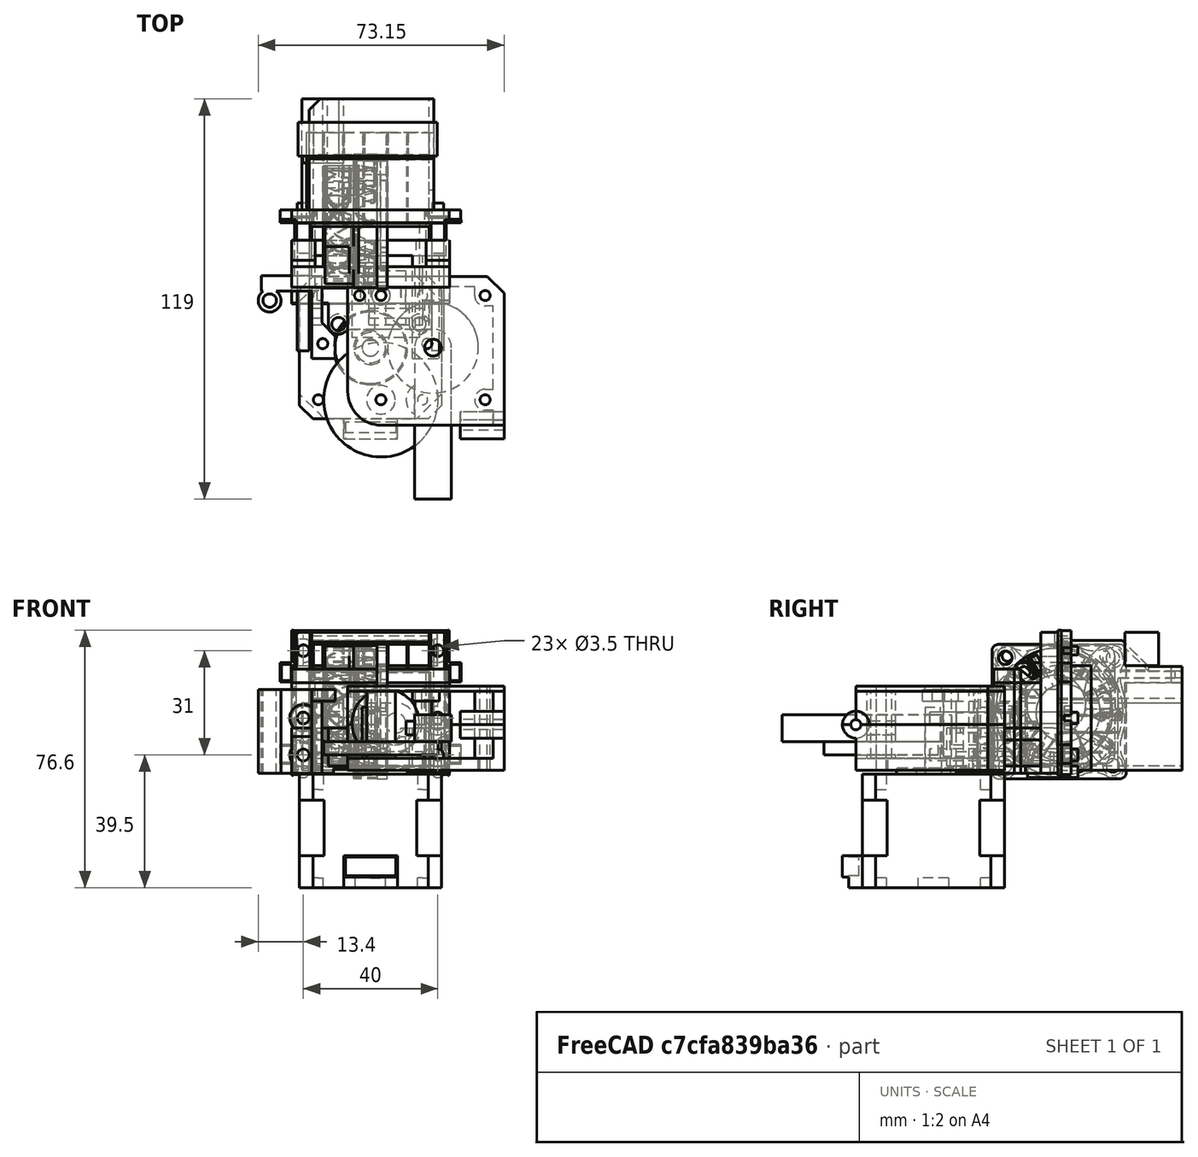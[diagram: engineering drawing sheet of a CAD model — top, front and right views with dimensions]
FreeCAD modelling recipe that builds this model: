
FCSTD DOCUMENT  (FreeCAD 0.17R9460 (Git))
Label: carriage_holder_proto_head
License: CC-BY 3.0
LicenseURL: http://creativecommons.org/licenses/by/3.0/
objects: Part::Box×86, Part::Cylinder×47, Part::MultiFuse×19, Part::Feature×16, Part::Cut×14, Mesh::Feature×6, App::DocumentObjectGroup×2, Part::Compound×2, Part::MultiCommon×1, Sketcher::SketchObject×1, Part::Extrusion×1, Part::Fillet×1, Drawing::FeatureViewPython×1, Drawing::FeaturePage×1, Part::Chamfer×1
note: 189 computed .brp shape members not serialized (recipe doc carries the construction recipe); baked Part::Feature solids carry a one-line shape summary decoded from their .brp

FEATURE [Part::Feature] Part__Feature  label="carriage holder base"
  Placement = pos=(0,4,-19.4607) rot=(1,0,0;1.5708rad)
  shape: bbox 53.76 x 4 x 42.8 mm, 26 faces (baked)
FEATURE [Part::Cylinder] Cylinder  label="cylinder for hole 1 - Motherboard"
  Angle = 360
  AttacherType = Attacher::AttachEngine3D
  Height = 15
  Placement = pos=(-20,6,17.5) rot=(1,0,0;1.5708rad)
  Radius = 1.75
FEATURE [Part::Cylinder] Cylinder001  label="cylinder for hole 2 - Motherboard"
  Angle = 360
  AttacherType = Attacher::AttachEngine3D
  Height = 15
  Placement = pos=(20,6,17.5) rot=(1,0,0;1.5708rad)
  Radius = 1.75
FEATURE [Part::Cylinder] Cylinder002  label="cylinder for hole 3 - Motherboard"
  Angle = 360
  AttacherType = Attacher::AttachEngine3D
  Height = 15
  Placement = pos=(-20,6,-18.5) rot=(1,0,0;1.5708rad)
  Radius = 1.75
FEATURE [Part::Cylinder] Cylinder003  label="cylinder for hole 4 - Motherboard"
  Angle = 360
  AttacherType = Attacher::AttachEngine3D
  Height = 15
  Placement = pos=(20,6,-18.5) rot=(1,0,0;1.5708rad)
  Radius = 1.75
FEATURE [Part::Cylinder] Cylinder008  label="cylinder for hole 9 - Groovemount L"
  Angle = 360
  AttacherType = Attacher::AttachEngine3D
  Height = 15
  Placement = pos=(-20,6,-2.5) rot=(1,0,0;1.5708rad)
  Radius = 1.75
FEATURE [Part::Cylinder] Cylinder009  label="cylinder for hole 10 - Groovemount R"
  Angle = 360
  AttacherType = Attacher::AttachEngine3D
  Height = 15
  Placement = pos=(20,6,-2.5) rot=(1,0,0;1.5708rad)
  Radius = 1.75
FEATURE [Part::Box] Box  label="shim L"
  AttacherType = Attacher::AttachEngine3D
  Height = 42
  Length = 4
  Placement = pos=(-22,-5,-19) rot=(0,0,1;0rad)
  Width = 6.1
FEATURE [Part::Box] Box001  label="shim R"
  AttacherType = Attacher::AttachEngine3D
  Height = 42
  Length = 4
  Placement = pos=(18,-5,-19) rot=(0,0,1;0rad)
  Width = 6.1
FEATURE [Part::Box] Box002  label="big aperture"
  AttacherType = Attacher::AttachEngine3D
  Height = 36
  Length = 32
  Placement = pos=(-16,-2,-18) rot=(0,0,1;0rad)
  Width = 10
FEATURE [Part::Cylinder] Cylinder010  label="cylinder for hole 2 nut seat"
  Angle = 360
  AttacherType = Attacher::AttachEngine3D
  Height = 2.5
  Placement = pos=(20,4,17.5) rot=(1,0,0;1.5708rad)
  Radius = 3.5
FEATURE [Part::Cylinder] Cylinder011  label="cylinder for hole 1 nut seat"
  Angle = 360
  AttacherType = Attacher::AttachEngine3D
  Height = 2.5
  Placement = pos=(-20,4,17.5) rot=(1,0,0;1.5708rad)
  Radius = 3.5
FEATURE [Part::Cylinder] Cylinder016  label="cylinder for hole 9 nut seat"
  Angle = 360
  AttacherType = Attacher::AttachEngine3D
  Height = 2
  Placement = pos=(-20,4,-2.5) rot=(1,0,0;1.5708rad)
  Radius = 3.5
FEATURE [Part::Cylinder] Cylinder017  label="cylinder for hole 10 nut seat"
  Angle = 360
  AttacherType = Attacher::AttachEngine3D
  Height = 2
  Placement = pos=(20,4,-2.5) rot=(1,0,0;1.5708rad)
  Radius = 3.5
FEATURE [Part::Box] Box003  label="shim subtractor L"
  AttacherType = Attacher::AttachEngine3D
  Height = 32
  Length = 3.4
  Placement = pos=(-27,1,-17) rot=(0,0,1;0rad)
  Width = 0.2
FEATURE [Part::Box] Box004  label="shim subtractor R"
  AttacherType = Attacher::AttachEngine3D
  Height = 32
  Length = 3.4
  Placement = pos=(23.6,1,-17) rot=(0,0,1;0rad)
  Width = 0.2
FEATURE [Part::Box] Box005  label="groovemount seat subtractor"
  AttacherType = Attacher::AttachEngine3D
  Height = 28
  Length = 36
  Placement = pos=(-18,-5,-17) rot=(0,0,1;0rad)
  Width = 5.2
FEATURE [Part::Box] Box006  label="Fan, screws and fan mount placeholder"
  AttacherType = Attacher::AttachEngine3D
  Height = 19
  Length = 35
  Placement = pos=(-17.5,0,3) rot=(0,0,1;0rad)
  Width = 35
FEATURE [Part::Box] Box007  label="Front intersector"
  AttacherType = Attacher::AttachEngine3D
  Height = 15
  Length = 56
  Placement = pos=(-28,-45,-20.5) rot=(0,0,1;0rad)
  Width = 49
FEATURE [Part::Cut] Cut001  label="groovemount E3D v6 high version"
FEATURE [Part::MultiCommon] Common  label="Front intersection"
  Shapes = -> [Cut001,Box007]
FEATURE [Part::Box] Box008  label="Left groovemount subtractor"
  AttacherType = Attacher::AttachEngine3D
  Height = 12
  Length = 10
  Placement = pos=(-32,-5,-17) rot=(0,0,1;0rad)
  Width = 5
FEATURE [Part::Box] Box009  label="Right groovemount subtractor"
  AttacherType = Attacher::AttachEngine3D
  Height = 12
  Length = 10
  Placement = pos=(22,-5,-17) rot=(0,0,1;0rad)
  Width = 5
FEATURE [Part::MultiFuse] Fusion  label="holes"
  Shapes = -> [Cylinder001,Cylinder,Cylinder008,Cylinder009,Box002,Cylinder010,Cylinder011,Cylinder016,Cylinder017,Box003,Box004,Box006,Box008,Box009]
FEATURE [Part::Box] Box010  label="Left groovemount adder"
  AttacherType = Attacher::AttachEngine3D
  Height = 11.25
  Length = 2
  Placement = pos=(-18.5,-5,-16.75) rot=(0,0,1;0rad)
  Width = 5
FEATURE [Part::Box] Box011  label="Right groovemount adder"
  AttacherType = Attacher::AttachEngine3D
  Height = 11.25
  Length = 2
  Placement = pos=(16.5,-5,-16.75) rot=(0,0,1;0rad)
  Width = 5
FEATURE [Part::MultiFuse] Fusion001  label="body"
  Shapes = -> [Part__Feature,Box001,Box,Common,Box010,Box011]
FEATURE [Part::Cut] Cut  label="carriage with shim and holes"
  Base = -> Fusion001
  Tool = -> Fusion
FEATURE [Part::Box] Box012  label="all area - outside "
  AttacherType = Attacher::AttachEngine3D
  Height = 38.6
  Length = 37
  Placement = pos=(-18.2,0,-18) rot=(0,0,1;0rad)
  Width = 37
FEATURE [Part::Box] Box014  label="safe area 1 - inside"
  AttacherType = Attacher::AttachEngine3D
  Height = 36
  Length = 25.4
  Placement = pos=(-8,0,-16.6) rot=(0,0,1;0rad)
  Width = 37
FEATURE [Part::Box] Box015  label="safe area 2 - inside"
  AttacherType = Attacher::AttachEngine3D
  Height = 16
  Length = 9
  Placement = pos=(-17,0,3.4) rot=(0,0,1;0rad)
  Width = 37
FEATURE [Part::Feature] Part__Feature001  label="carriage holder base001"
  Placement = pos=(0,4,-19.4607) rot=(1,0,0;1.5708rad)
  shape: bbox 53.76 x 4 x 42.8 mm, 26 faces (baked)
FEATURE [Part::Box] Box016  label="top remover"
  AttacherType = Attacher::AttachEngine3D
  Height = 60
  Length = 60
  Placement = pos=(-31,0,-29) rot=(0,0,1;0rad)
  Width = 0.1
FEATURE [Part::Box] Box017  label="recess"
  AttacherType = Attacher::AttachEngine3D
  Height = 6
  Length = 6
  Placement = pos=(-20.2,18,2) rot=(0,0,1;0rad)
  Width = 19
FEATURE [Part::Box] Box018  label="raspicam collision area - outside001"
  AttacherType = Attacher::AttachEngine3D
  Height = 20
  Length = 11
  Placement = pos=(-20.4,0,-18) rot=(0,0,1;0rad)
  Width = 37
FEATURE [Part::Cut] Cut004  label="raspicam_extra"
  Base = -> Box018
  Tool = -> Box017
FEATURE [Part::Box] Box020  label="recess_base"
  AttacherType = Attacher::AttachEngine3D
  Height = 6
  Length = 4
  Placement = pos=(-18.2,18,2) rot=(0,0,1;0rad)
  Width = 2
FEATURE [Part::Box] Box021  label="support for recess base X1"
  AttacherType = Attacher::AttachEngine3D
  Height = 0.4
  Length = 4
  Placement = pos=(-17,0.1,9) rot=(0,0,1;0rad)
  Width = 18
FEATURE [Part::Box] Box022  label="support for recess base Y1"
  AttacherType = Attacher::AttachEngine3D
  Height = 6
  Length = 0.4
  Placement = pos=(-13.2,0.1,3.4) rot=(0,0,1;0rad)
  Width = 18
FEATURE [Part::Box] Box023  label="raspicam collision area - outside lower"
  AttacherType = Attacher::AttachEngine3D
  Height = 20
  Length = 9
  Placement = pos=(-18.4,20,-18) rot=(0,0,1;0rad)
  Width = 34
FEATURE [Part::Box] Box024  label="recess001"
  AttacherType = Attacher::AttachEngine3D
  Height = 6
  Length = 6
  Placement = pos=(-20.2,18,2) rot=(0,0,1;0rad)
  Width = 19
FEATURE [Part::Box] Box025  label="recess wall 1"
  AttacherType = Attacher::AttachEngine3D
  Height = 6
  Length = 1.4
  Placement = pos=(-14.2,18,2) rot=(0,0,1;0rad)
  Width = 19
FEATURE [Part::Box] Box026  label="recess wall 2"
  AttacherType = Attacher::AttachEngine3D
  Height = 1.4
  Length = 5.4
  Placement = pos=(-18.2,18,8) rot=(0,0,1;0rad)
  Width = 19
FEATURE [Part::Box] Box027  label="Raspicam chamfer"
  AttacherType = Attacher::AttachEngine3D
  Height = 15
  Length = 13
  Placement = pos=(-22,30,7) rot=(0,0,1;0.785398rad)
  Width = 10
FEATURE [Part::Box] Box028  label="Rear panel chamfer"
  AttacherType = Attacher::AttachEngine3D
  Height = 11
  Length = 41.4
  Placement = pos=(-21.6,27,12.81) rot=(1,0,0;0.785398rad)
  Width = 10
FEATURE [Part::Box] Box029  label="Rear panel recess template"
  AttacherType = Attacher::AttachEngine3D
  Height = 31
  Length = 1.4
  Placement = pos=(17.4,0,-18) rot=(0,0,1;0rad)
  Width = 10
FEATURE [Part::Box] Box030  label="Rear panel recess"
  AttacherType = Attacher::AttachEngine3D
  Height = 7.8
  Length = 41.4
  Placement = pos=(-21.6,27,12.8) rot=(0,0,1;0rad)
  Width = 10
FEATURE [Part::MultiFuse] Fusion004  label="Extra subtractions"
  Shapes = -> [Box027,Box030]
FEATURE [Part::Box] Box031  label="Rear panel chamfer template"
  AttacherType = Attacher::AttachEngine3D
  Height = 10
  Length = 41.4
  Placement = pos=(-21.6,20,13) rot=(0,0,1;0rad)
  Width = 10
FEATURE [Part::Box] Box032  label="Rear panel wall vs front"
  AttacherType = Attacher::AttachEngine3D
  Height = 1.4
  Length = 35.4
  Placement = pos=(-18,27,11.4) rot=(0,0,1;0rad)
  Width = 10
FEATURE [Sketcher::SketchObject] Sketch
  MapMode = 5
  Placement = pos=(-19,27,11.4) rot=(0.57735,0.57735,0.57735;2.0944rad)
  sketch-geometry (4):
    g0: LineSegment StartX=-6.61145 StartY=8.01145 StartZ=0 EndX=0 EndY=1.4 EndZ=0
    g1: LineSegment StartX=0 StartY=1.4 StartZ=0 EndX=0 EndY=0 EndZ=0
    g2: LineSegment StartX=0 StartY=0 StartZ=0 EndX=-8.01145 EndY=8.01145 EndZ=0
    g3: LineSegment StartX=-8.01145 StartY=8.01145 StartZ=0 EndX=-6.61145 EndY=8.01145 EndZ=0
  constraints (11):
    c: PointOnObject(g0,g-2)
    c: Coincident(g0,g1)
    c: Coincident(g1,g-1)
    c: Coincident(g1,g2)
    c: Coincident(g2,g3)
    c: Coincident(g3,g0)
    c: DistanceY(g1,g1) = 1.4
    c: DistanceX(g3,g3) = 1.4
    c: Parallel(g0,g2)
    c: Angle(g-1,g2) = 2.35619
    c: Distance(g0,g0) = 9.35
FEATURE [Part::Extrusion] Extrude  label="Rear panel angled"
  Base = -> Sketch
  Dir = (36,0,0)
  DirMode = 0
  FaceMakerClass = Part::FaceMakerExtrusion
  LengthFwd = 0
  LengthRev = 0
  Placement = pos=(1,0,0) rot=(0,0,1;0rad)
  Solid = true
  Symmetric = false
FEATURE [Part::Box] Box033  label="support X1 for rear panel angled"
  AttacherType = Attacher::AttachEngine3D
  Height = 0.4
  Length = 36.4
  Placement = pos=(-19,0.1,11.4) rot=(0,0,1;0rad)
  Width = 27
FEATURE [Part::Box] Box034  label="support Y1 for rear panel angled"
  AttacherType = Attacher::AttachEngine3D
  Height = 9
  Length = 0.4
  Placement = pos=(-14.2,0.1,11.4) rot=(0,0,1;0rad)
  Width = 27
FEATURE [Part::Box] Box035  label="support Y2 for rear panel angled"
  AttacherType = Attacher::AttachEngine3D
  Height = 9
  Length = 0.4
  Placement = pos=(-8.2,0.1,11.4) rot=(0,0,1;0rad)
  Width = 27
FEATURE [Part::Box] Box036  label="support Y3 for rear panel angled"
  AttacherType = Attacher::AttachEngine3D
  Height = 9
  Length = 0.4
  Placement = pos=(4.8,0.1,11.4) rot=(0,0,1;0rad)
  Width = 27
FEATURE [Part::Box] Box037  label="support Y4 for rear panel angled"
  AttacherType = Attacher::AttachEngine3D
  Height = 9
  Length = 0.4
  Placement = pos=(-2.2,0.1,11.4) rot=(0,0,1;0rad)
  Width = 27
FEATURE [Part::Box] Box038  label="support Y5 for rear panel angled"
  AttacherType = Attacher::AttachEngine3D
  Height = 9
  Length = 0.4
  Placement = pos=(10.8,0.1,11.4) rot=(0,0,1;0rad)
  Width = 27
FEATURE [Part::MultiFuse] Fusion005  label="supports for rear panel angled"
  Shapes = -> [Box033,Box037,Box036,Box035,Box034,Box038]
FEATURE [Part::Cut] Cut006  label="supports for rear panel angled - chamfered"
  Base = -> Fusion005
  Tool = -> Box028
FEATURE [Mesh::Feature] chinese_long_distance_hotend
  Placement = pos=(1.6,0,1.6) rot=(0,1,0;3.14159rad)
FEATURE [Part::Box] Box039  label="recess_base 2"
  AttacherType = Attacher::AttachEngine3D
  Height = 20
  Length = 12.2
  Placement = pos=(-20.2,18,-18) rot=(0,0,1;0rad)
  Width = 2
FEATURE [Part::Box] Box040  label="top on raspicam area "
  AttacherType = Attacher::AttachEngine3D
  Height = 20
  Length = 11
  Placement = pos=(-17,-16,-16.6) rot=(0,0,1;0rad)
  Width = 34
FEATURE [Part::Box] Box041  label="support for recess base X2"
  AttacherType = Attacher::AttachEngine3D
  Height = 0.4
  Length = 9
  Placement = pos=(-17,0.1,3) rot=(0,0,1;0rad)
  Width = 18
FEATURE [Part::Box] Box042  label="support for recess base X3"
  AttacherType = Attacher::AttachEngine3D
  Height = 0.4
  Length = 10
  Placement = pos=(-18,0.1,-2) rot=(0,0,1;0rad)
  Width = 18
FEATURE [Part::Box] Box043  label="support for recess base X4"
  AttacherType = Attacher::AttachEngine3D
  Height = 0.4
  Length = 10
  Placement = pos=(-18,0.1,-13) rot=(0,0,1;0rad)
  Width = 18
FEATURE [Part::Box] Box044  label="support for recess base X5"
  AttacherType = Attacher::AttachEngine3D
  Height = 0.4
  Length = 9
  Placement = pos=(-17,0.1,-7) rot=(0,0,1;0rad)
  Width = 18
FEATURE [Part::Box] Box045  label="support for recess base Y2"
  AttacherType = Attacher::AttachEngine3D
  Height = 20
  Length = 0.4
  Placement = pos=(-8.4,0.1,-16.6) rot=(0,0,1;0rad)
  Width = 18
FEATURE [Part::MultiFuse] Fusion006  label="supports for recess base"
  Shapes = -> [Box041,Box045,Box044,Box042,Box043,Box021,Box022]
FEATURE [Part::Cylinder] Cylinder018  label="cylinder for hole 2 nut seat001"
  Angle = 360
  AttacherType = Attacher::AttachEngine3D
  Height = 2.5
  Placement = pos=(20,4,17.5) rot=(1,0,0;1.5708rad)
  Radius = 3.5
FEATURE [Part::Cylinder] Cylinder019  label="cylinder for hole 1 nut seat001"
  Angle = 360
  AttacherType = Attacher::AttachEngine3D
  Height = 2.5
  Placement = pos=(-20,4,17.5) rot=(1,0,0;1.5708rad)
  Radius = 3.5
FEATURE [Part::Cylinder] Cylinder020  label="cylinder for hole 1 - Motherboard001"
  Angle = 360
  AttacherType = Attacher::AttachEngine3D
  Height = 15
  Placement = pos=(-20,6,17.5) rot=(1,0,0;1.5708rad)
  Radius = 1.75
FEATURE [Part::Cylinder] Cylinder021  label="cylinder for hole 2 - Motherboard001"
  Angle = 360
  AttacherType = Attacher::AttachEngine3D
  Height = 15
  Placement = pos=(20,6,17.5) rot=(1,0,0;1.5708rad)
  Radius = 1.75
FEATURE [Part::Box] Box046  label="shim R001"
  AttacherType = Attacher::AttachEngine3D
  Height = 42
  Length = 5
  Placement = pos=(17.5,-5,-19) rot=(0,0,1;0rad)
  Width = 5.1
FEATURE [Part::Box] Box047  label="shim L001"
  AttacherType = Attacher::AttachEngine3D
  Height = 42
  Length = 5
  Placement = pos=(-22.5,-5,-19) rot=(0,0,1;0rad)
  Width = 5.1
FEATURE [Part::Box] Box048  label="shim back"
  AttacherType = Attacher::AttachEngine3D
  Height = 3
  Length = 44
  Placement = pos=(-22,-1,20) rot=(0,0,1;0rad)
  Width = 1.1
FEATURE [Part::Box] Box049  label="shim front"
  AttacherType = Attacher::AttachEngine3D
  Height = 2
  Length = 44
  Placement = pos=(-22,-1,-19) rot=(0,0,1;0rad)
  Width = 1.1
FEATURE [Part::MultiFuse] Fusion007  label="superstructure"
  Shapes = -> [Box046,Box048,Box047,Box049]
FEATURE [Part::Cylinder] Cylinder022  label="cylinder for hole 1 - Motherboard002"
  Angle = 360
  AttacherType = Attacher::AttachEngine3D
  Height = 44
  Placement = pos=(-20,6,17.5) rot=(1,0,0;1.5708rad)
  Radius = 1.75
FEATURE [Part::Cylinder] Cylinder023  label="cylinder for hole 2 - Motherboard002"
  Angle = 360
  AttacherType = Attacher::AttachEngine3D
  Height = 44
  Placement = pos=(20,6,17.5) rot=(1,0,0;1.5708rad)
  Radius = 1.75
FEATURE [Part::Cylinder] Cylinder024  label="cylinder for hole 9 - Groovemount L001"
  Angle = 360
  AttacherType = Attacher::AttachEngine3D
  Height = 44
  Placement = pos=(-20,6,-2.5) rot=(1,0,0;1.5708rad)
  Radius = 1.75
FEATURE [Part::Cylinder] Cylinder025  label="cylinder for hole 10 - Groovemount R001"
  Angle = 360
  AttacherType = Attacher::AttachEngine3D
  Height = 44
  Placement = pos=(20,6,-2.5) rot=(1,0,0;1.5708rad)
  Radius = 1.75
FEATURE [Part::Cylinder] Cylinder026  label="cylinder for hole 9 nut seat001"
  Angle = 360
  AttacherType = Attacher::AttachEngine3D
  Height = 2
  Placement = pos=(-20,4,-2.5) rot=(1,0,0;1.5708rad)
  Radius = 3.5
FEATURE [Part::Cylinder] Cylinder027  label="cylinder for hole 10 nut seat001"
  Angle = 360
  AttacherType = Attacher::AttachEngine3D
  Height = 2
  Placement = pos=(20,4,-2.5) rot=(1,0,0;1.5708rad)
  Radius = 3.5
FEATURE [Part::Cylinder] Cylinder028  label="cylinder for hole 9 - Groovemount L002"
  Angle = 360
  AttacherType = Attacher::AttachEngine3D
  Height = 15
  Placement = pos=(-20,6,-2.5) rot=(1,0,0;1.5708rad)
  Radius = 1.75
FEATURE [Part::Cylinder] Cylinder029  label="cylinder for hole 10 - Groovemount R002"
  Angle = 360
  AttacherType = Attacher::AttachEngine3D
  Height = 15
  Placement = pos=(20,6,-2.5) rot=(1,0,0;1.5708rad)
  Radius = 1.75
FEATURE [Part::Cylinder] Cylinder030  label="cylinder for hole 3 - Motherboard001"
  Angle = 360
  AttacherType = Attacher::AttachEngine3D
  Height = 15
  Placement = pos=(-20,6,-13.5) rot=(1,0,0;1.5708rad)
  Radius = 1.75
FEATURE [Part::Cylinder] Cylinder031  label="cylinder for hole 4 - Motherboard001"
  Angle = 360
  AttacherType = Attacher::AttachEngine3D
  Height = 15
  Placement = pos=(20,6,-13.5) rot=(1,0,0;1.5708rad)
  Radius = 1.75
FEATURE [Part::Cylinder] Cylinder032  label="cylinder for hole 9 nut seat002"
  Angle = 360
  AttacherType = Attacher::AttachEngine3D
  Height = 2
  Placement = pos=(-20,4,-13.5) rot=(1,0,0;1.5708rad)
  Radius = 3.5
FEATURE [Part::Cylinder] Cylinder033  label="cylinder for hole 10 nut seat002"
  Angle = 360
  AttacherType = Attacher::AttachEngine3D
  Height = 2
  Placement = pos=(20,4,-13.5) rot=(1,0,0;1.5708rad)
  Radius = 3.5
FEATURE [Part::MultiFuse] Fusion002  label="safe area holes"
  Shapes = -> [Box014,Box015,Box016,Box023,Box024,Box028,Fusion004,Box040,Cylinder018,Cylinder019,Cylinder020,Cylinder021,Cylinder027,Cylinder026,Cylinder028,Cylinder029,Cylinder030,Cylinder031,Cylinder032,Cylinder033]
FEATURE [Part::Cut] Cut002  label="safe area protector"
  Base = -> Box012
  Tool = -> Fusion002
FEATURE [Part::Cut] Cut003  label="carriage holder base with safe area aperture"
  Base = -> Part__Feature001
  Tool = -> Fusion002
FEATURE [Part::Cylinder] Cylinder034  label="cylinder for hole 3 - Motherboard002"
  Angle = 360
  AttacherType = Attacher::AttachEngine3D
  Height = 44
  Placement = pos=(-20,6,-13.5) rot=(1,0,0;1.5708rad)
  Radius = 1.75
FEATURE [Part::Cylinder] Cylinder035  label="cylinder for hole 4 - Motherboard002"
  Angle = 360
  AttacherType = Attacher::AttachEngine3D
  Height = 44
  Placement = pos=(20,6,-13.5) rot=(1,0,0;1.5708rad)
  Radius = 1.75
FEATURE [Part::MultiFuse] Fusion008  label="superstructure holes"
  Shapes = -> [Cylinder022,Cylinder023,Cylinder024,Cylinder025,Cylinder034,Cylinder035]
FEATURE [Part::Cut] Cut007  label="superstructure with holes"
  Base = -> Fusion007
  Tool = -> Fusion008
FEATURE [Mesh::Feature] k3dpkr_rc_1_0_x_carriage  label="k3dpkr-rc-1.0-x-carriage"
  Placement = pos=(-466,-28,-403) rot=(-1,0,0;1.5708rad)
FEATURE [Part::Box] Box050  label="coldend carriage plate"
  AttacherType = Attacher::AttachEngine3D
  Height = 17
  Length = 47
  Placement = pos=(-23.5,-19,-9) rot=(0,0,1;0rad)
  Width = 6.1
FEATURE [Part::Cylinder] Cylinder036  label="coldend carriage plate hole"
  Angle = 360
  AttacherType = Attacher::AttachEngine3D
  Height = 34
  Placement = pos=(4.5,0,-4) rot=(1,0,0;1.5708rad)
  Radius = 10
FEATURE [Part::MultiFuse] Fusion009  label="coldend carriage holes"
  Shapes = -> [Cylinder024,Cylinder025,Cylinder034,Cylinder035,Cylinder036]
FEATURE [Part::Box] Box051  label="coldend cariage structure R"
  AttacherType = Attacher::AttachEngine3D
  Height = 17
  Length = 7
  Placement = pos=(16.5,-12.9,-9) rot=(0,0,1;0rad)
  Width = 7.9
FEATURE [Part::Box] Box052  label="coldend cariage structure L"
  AttacherType = Attacher::AttachEngine3D
  Height = 17
  Length = 7
  Placement = pos=(-23.5,-12.9,-9) rot=(0,0,1;0rad)
  Width = 7.9
FEATURE [Part::MultiFuse] Fusion010  label="coldend attach structure"
  Shapes = -> [Box051,Box052,Box050]
FEATURE [Part::Cut] Cut008  label="coldend attach structure with holes"
  Base = -> Fusion010
  Tool = -> Fusion009
FEATURE [Part::Feature] Part__Feature200  label="Part 003"
  shape: bbox 30 x 30.5 x 10.5 mm, 33 faces (baked)
FEATURE [Part::Feature] Part__Feature201  label="Part 004"
  shape: bbox 28.66 x 28.3 x 8.25 mm, 39 faces (baked)
FEATURE [Part::MultiFuse] Fusion014  label="30x30x10 coldend fan"
  Placement = pos=(-14,2,-1) rot=(0,1,0;1.5708rad)
  Shapes = -> [Part__Feature201,Part__Feature200]
FEATURE [Part::Cylinder] Cylinder037  label="jhead hole"
  Angle = 360
  AttacherType = Attacher::AttachEngine3D
  Height = 34
  Placement = pos=(4.5,0,-4) rot=(1,0,0;1.5708rad)
  Radius = 6
FEATURE [Part::Box] Box053  label="jhead retention plate body"
  AttacherType = Attacher::AttachEngine3D
  Height = 27
  Length = 47
  Placement = pos=(-23.5,-24,-19) rot=(0,0,1;0rad)
  Width = 5
FEATURE [Part::Box] Box054  label="jhead retention plate chamfer L"
  AttacherType = Attacher::AttachEngine3D
  Height = 14
  Length = 37
  Placement = pos=(-32.5,-24,-17) rot=(0,1,0;0.314159rad)
  Width = 5
FEATURE [Part::Box] Box055  label="jhead retention plate chamfer R"
  AttacherType = Attacher::AttachEngine3D
  Height = 11
  Length = 22
  Placement = pos=(16.5,-24,-27) rot=(0,-1,0;0.785398rad)
  Width = 5
FEATURE [Part::Box] Box056  label="jhead retention plate slide in hole"
  AttacherType = Attacher::AttachEngine3D
  Height = 31
  Length = 12
  Placement = pos=(-1.5,-24,-35) rot=(0,0,1;0rad)
  Width = 5
FEATURE [Part::MultiFuse] Fusion015  label="jhead retention plate holes"
  Shapes = -> [Cylinder025,Cylinder024,Cylinder037,Box054,Box055,Box056]
FEATURE [Part::Cut] Cut009  label="jhead retention plate with holes"
  Base = -> Box053
  Tool = -> Fusion015
FEATURE [Part::Fillet] Fillet  label="jhead retention plate with holes and fillets"
  Base = -> Cut009
  Edges = 6 edges r=3: [Edge2,Edge4,Edge15,Edge24,Edge27,Edge28]
FEATURE [Mesh::Feature] Pico
  Placement = pos=(12,36,-11) rot=(0,0,1;3.14159rad)
FEATURE [Part::Box] Box057  label="jhead lock plate"
  AttacherType = Attacher::AttachEngine3D
  Height = 11
  Length = 47
  Placement = pos=(-23.5,-24,-18) rot=(0,0,1;0rad)
  Width = 5
FEATURE [Part::Cut] Cut010  label="jhead lock plate coupled with retention plate"
  Base = -> Box057
  Placement = pos=(0,0,-1) rot=(0,0,1;0rad)
  Tool = -> Fillet
FEATURE [Part::MultiFuse] Fusion016  label="jhead lock plate holes"
  Shapes = -> [Cylinder037,Cylinder035,Cylinder034]
FEATURE [Part::Cut] Cut011  label="jhead retention plates - lock and retention"
  Base = -> Cut010
  Tool = -> Fusion016
FEATURE [Part::Box] Box058  label="support for lock pins XL1"
  AttacherType = Attacher::AttachEngine3D
  Height = 0.4
  Length = 5
  Placement = pos=(-26.8,0.1,8.2) rot=(0,0,1;0rad)
  Width = 1
FEATURE [Part::Box] Box059  label="support for lock pins YL1"
  AttacherType = Attacher::AttachEngine3D
  Height = 43.2
  Length = 0.4
  Placement = pos=(-23.4,0.1,-19.6) rot=(0,0,1;0rad)
  Width = 1
FEATURE [Part::Box] Box060  label="support for lock pins YR1"
  AttacherType = Attacher::AttachEngine3D
  Height = 43.2
  Length = 0.4
  Placement = pos=(23,0.1,-19.6) rot=(0,0,1;0rad)
  Width = 1
FEATURE [Part::Box] Box061  label="support for lock pins YL2"
  AttacherType = Attacher::AttachEngine3D
  Height = 5.7
  Length = 0.4
  Placement = pos=(-26.9,0.1,8.2) rot=(0,0,1;0rad)
  Width = 1
FEATURE [Part::Box] Box062  label="support for lock pins XL2"
  AttacherType = Attacher::AttachEngine3D
  Height = 0.4
  Length = 5
  Placement = pos=(-26.8,0.1,13.5) rot=(0,0,1;0rad)
  Width = 1
FEATURE [Part::Box] Box063  label="support for lock pins XL3"
  AttacherType = Attacher::AttachEngine3D
  Height = 0.4
  Length = 5
  Placement = pos=(-26.8,0.1,-10.8) rot=(0,0,1;0rad)
  Width = 1
FEATURE [Part::Box] Box064  label="support for lock pins XL4"
  AttacherType = Attacher::AttachEngine3D
  Height = 0.4
  Length = 5
  Placement = pos=(-26.8,0.1,-16.1) rot=(0,0,1;0rad)
  Width = 1
FEATURE [Part::Box] Box065  label="support for lock pins YL3"
  AttacherType = Attacher::AttachEngine3D
  Height = 5.7
  Length = 0.4
  Placement = pos=(-26.9,0.1,-16.1) rot=(0,0,1;0rad)
  Width = 1
FEATURE [Part::Box] Box066  label="support for lock pins XR1"
  AttacherType = Attacher::AttachEngine3D
  Height = 0.4
  Length = 5
  Placement = pos=(22,0.1,8.2) rot=(0,0,1;0rad)
  Width = 1
FEATURE [Part::Box] Box067  label="support for lock pins XR2"
  AttacherType = Attacher::AttachEngine3D
  Height = 0.4
  Length = 5
  Placement = pos=(22,0.1,13.5) rot=(0,0,1;0rad)
  Width = 1
FEATURE [Part::Box] Box068  label="support for lock pins XR3"
  AttacherType = Attacher::AttachEngine3D
  Height = 0.4
  Length = 5
  Placement = pos=(22,0.1,-10.8) rot=(0,0,1;0rad)
  Width = 1
FEATURE [Part::Box] Box069  label="support for lock pins XR4"
  AttacherType = Attacher::AttachEngine3D
  Height = 0.4
  Length = 5
  Placement = pos=(22,0.1,-16.1) rot=(0,0,1;0rad)
  Width = 1
FEATURE [Part::Box] Box070  label="support for lock pins YR2"
  AttacherType = Attacher::AttachEngine3D
  Height = 5.7
  Length = 0.4
  Placement = pos=(26.6,0.1,8.2) rot=(0,0,1;0rad)
  Width = 1
FEATURE [Part::Box] Box071  label="support for lock pins YR3"
  AttacherType = Attacher::AttachEngine3D
  Height = 5.7
  Length = 0.4
  Placement = pos=(26.6,0.1,-16.1) rot=(0,0,1;0rad)
  Width = 1
FEATURE [Part::MultiFuse] Fusion017  label="support for lock pins"
  Shapes = -> [Box059,Box070,Box065,Box068,Box062,Box063,Box060,Box061,Box066,Box067,Box064,Box069,Box071,Box058]
FEATURE [Part::MultiFuse] Fusion003  label="carriage holder base with safe area protector"
  Shapes = -> [Cut003,Cut002,Box020,Box025,Box026,Box032,Extrude,Fusion006,Fusion017]
FEATURE [Part::Cut] Cut005  label="carriage holder base with safe area protector and extra subtractions"
  Base = -> Fusion003
  Tool = -> Box027
FEATURE [Drawing::FeatureViewPython] ViewCut005  # drawing view (typed FeaturePython)
  AlwaysOn = false
  Direction = (0,0,0)
  FillStyle = 0
  FontSize = 12
  LineSpacing = 0
  LineStyle = 0
  LineWidth = 0.35
  Rotation = 0
  Scale = 20
  Source = -> Cut005
  ViewResult = <blob: 93087 chars omitted>
  Visible = false
  X = 200
  Y = 100
FEATURE [Drawing::FeaturePage] Page
  EditableTexts = AUTHOR NAME | CREATION DATE | SUPERVISOR NAME | CHECK DATE | SCALE | WEIGHT | NUMBER | SHEET | TITLE | SUBTITLE
  Group = -> [ViewCut005]
  Template = <path>
FEATURE [Part::Cylinder] Cylinder038  label="cylinder for hole 9 - Groovemount L003"
  Angle = 360
  AttacherType = Attacher::AttachEngine3D
  Height = 44
  Placement = pos=(-20,6,-2.5) rot=(1,0,0;1.5708rad)
  Radius = 1.75
FEATURE [Part::Cylinder] Cylinder039  label="cylinder for hole 10 - Groovemount R003"
  Angle = 360
  AttacherType = Attacher::AttachEngine3D
  Height = 44
  Placement = pos=(20,6,-2.5) rot=(1,0,0;1.5708rad)
  Radius = 1.75
FEATURE [Part::Cylinder] Cylinder040  label="cylinder for hole 3 - Motherboard003"
  Angle = 360
  AttacherType = Attacher::AttachEngine3D
  Height = 44
  Placement = pos=(-20,6,-13.5) rot=(1,0,0;1.5708rad)
  Radius = 1.75
FEATURE [Part::Cylinder] Cylinder041  label="cylinder for hole 4 - Motherboard003"
  Angle = 360
  AttacherType = Attacher::AttachEngine3D
  Height = 44
  Placement = pos=(20,6,-13.5) rot=(1,0,0;1.5708rad)
  Radius = 1.75
FEATURE [Part::Box] Box072  label="coldend carriage plate001"
  AttacherType = Attacher::AttachEngine3D
  Height = 31
  Length = 47
  Placement = pos=(-23.5,-19,-19) rot=(0,0,1;0rad)
  Width = 6.1
FEATURE [Part::Cylinder] Cylinder042  label="coldend carriage plate hole001"
  Angle = 360
  AttacherType = Attacher::AttachEngine3D
  Height = 34
  Placement = pos=(4.5,0,-4) rot=(1,0,0;1.5708rad)
  Radius = 10
FEATURE [Part::Box] Box073  label="coldend cariage structure R001"
  AttacherType = Attacher::AttachEngine3D
  Height = 31
  Length = 7
  Placement = pos=(16.5,-12.9,-19) rot=(0,0,1;0rad)
  Width = 1.9
FEATURE [Part::Box] Box074  label="coldend cariage structure L001"
  AttacherType = Attacher::AttachEngine3D
  Height = 31
  Length = 7
  Placement = pos=(-23.5,-12.9,-19) rot=(0,0,1;0rad)
  Width = 1.9
FEATURE [App::DocumentObjectGroup] Gruppo  label="Unused"
  Group = -> [Cylinder002,Cylinder003,Cut,Box005,Cut004,Box029,Box031,Box039,Cut006,Box072,Box074,Box073,Cylinder038,Cylinder039,Cylinder041,Cylinder042]
FEATURE [Mesh::Feature] _015_Blower_Fan  label="5015_Blower_Fan"
  Placement = pos=(17,-16,21) rot=(0,0,1;3.14159rad)
FEATURE [Mesh::Feature] hexagon_ruotato  label="hexagon AO hotend"
  Placement = pos=(7.3,-14.2,-4) rot=(0,-1,0;1.71042rad)
FEATURE [Part::Cylinder] Cylinder043  label="cylinder for hole 9 - Groovemount L004"
  Angle = 360
  AttacherType = Attacher::AttachEngine3D
  Height = 44
  Placement = pos=(-20,6,-2.5) rot=(1,0,0;1.5708rad)
  Radius = 1.75
FEATURE [Part::Cylinder] Cylinder044  label="cylinder for hole 10 - Groovemount R004"
  Angle = 360
  AttacherType = Attacher::AttachEngine3D
  Height = 44
  Placement = pos=(20,6,-2.5) rot=(1,0,0;1.5708rad)
  Radius = 1.75
FEATURE [Part::Cylinder] Cylinder045  label="jhead hole001"
  Angle = 360
  AttacherType = Attacher::AttachEngine3D
  Height = 34
  Placement = pos=(7.5,0,-4) rot=(1,0,0;1.5708rad)
  Radius = 6
FEATURE [Part::Box] Box075  label="jhead retention plate body001"
  AttacherType = Attacher::AttachEngine3D
  Height = 25
  Length = 26
  Placement = pos=(-3.5,-9.6,-19) rot=(0,0,1;0rad)
  Width = 4.6
FEATURE [Part::Box] Box078  label="jhead retention plate slide in hole001"
  AttacherType = Attacher::AttachEngine3D
  Height = 12
  Length = 17
  Placement = pos=(-9.5,-14.6,-10) rot=(0,0,1;0rad)
  Width = 17.6
FEATURE [Part::Cylinder] Cylinder046  label="cylinder for hole 4 - Motherboard004"
  Angle = 360
  AttacherType = Attacher::AttachEngine3D
  Height = 44
  Placement = pos=(20,6,-13.5) rot=(1,0,0;1.5708rad)
  Radius = 1.75
FEATURE [Part::Box] Box079  label="fan bracket left"
  AttacherType = Attacher::AttachEngine3D
  Height = 25
  Length = 5
  Placement = pos=(-22.5,-15.6,-19) rot=(0,0,1;0rad)
  Width = 10.6
FEATURE [Part::Box] Box080  label="blower bracket base"
  AttacherType = Attacher::AttachEngine3D
  Height = 25
  Length = 15
  Placement = pos=(-32.5,-20.2,-19) rot=(0,0,1;0rad)
  Width = 4.6
FEATURE [Part::Box] Box081  label="fan bracket retention plate joiner lower"
  AttacherType = Attacher::AttachEngine3D
  Height = 25
  Length = 2
  Placement = pos=(-3.5,-19.6,-19) rot=(0,0,1;0rad)
  Width = 10.6
FEATURE [Part::Box] Box082  label="retention hexagon head slide in hole"
  AttacherType = Attacher::AttachEngine3D
  Height = 16
  Length = 2
  Placement = pos=(-3.5,-14.6,-12) rot=(0,0,1;0rad)
  Width = 24.6
FEATURE [Part::Cylinder] Cylinder047  label="30x30 fan hole"
  Angle = 360
  AttacherType = Attacher::AttachEngine3D
  Height = 21
  Placement = pos=(-24,-10,11) rot=(0,1,0;1.5708rad)
  Radius = 1.75
FEATURE [App::DocumentObjectGroup] Gruppo001  label="unused hexagon"
  Group = -> [Box081]
FEATURE [Part::Box] Box083  label="fan bracket retention plate joint"
  AttacherType = Attacher::AttachEngine3D
  Height = 3
  Length = 14
  Placement = pos=(-17.5,-9.6,-19) rot=(0,0,1;0rad)
  Width = 4.6
FEATURE [Part::Cylinder] Cylinder048  label="blower retention"
  Angle = 360
  AttacherType = Attacher::AttachEngine3D
  Height = 25
  Placement = pos=(-30,-23,-19) rot=(0,0,1;0rad)
  Radius = 3.4
FEATURE [Part::Cylinder] Cylinder049  label="blower screw"
  Angle = 360
  AttacherType = Attacher::AttachEngine3D
  Height = 42
  Placement = pos=(-30,-23,-19) rot=(0,0,1;0rad)
  Radius = 2
FEATURE [Part::Feature] Part__Feature202  label="e3D Titan Extruder v5"
  shape: bbox 46.5 x 48.2 x 13.5 mm, 40 faces (baked)
FEATURE [Part::Feature] Part__Feature203  label="e3D Titan Extruder v006"
  shape: bbox 46.5 x 44.2 x 1.5 mm, 14 faces (baked)
FEATURE [Part::Feature] Part__Feature204  label="e3D Titan Extruder v007"
  shape: bbox 34 x 34 x 20 mm, 8 faces (baked)
FEATURE [Part::Feature] Part__Feature205  label="e3D Titan Extruder v008"
  shape: bbox 8 x 15.75 x 10 mm, 11 faces (baked)
FEATURE [Part::Feature] Part__Feature206  label="e3D Titan Extruder v009"
  shape: bbox 26.5 x 44.2 x 10 mm, 23 faces (baked)
FEATURE [Part::Feature] Part__Feature207  label="e3D Titan Extruder v010"
  shape: bbox 5 x 5 x 8.5 mm, 3 faces (baked)
FEATURE [Part::Feature] Part__Feature208  label="e3D Titan Extruder v011"
  shape: bbox 13.47 x 50.5 x 8 mm, 10 faces (baked)
FEATURE [Part::Feature] Part__Feature209  label="e3D Titan Extruder v012"
  shape: bbox 13 x 8 x 4.001 mm, 6 faces (baked)
FEATURE [Part::Compound] e3D_Titan_Extruder_v5
  Links = -> [Part__Feature202,Part__Feature203,Part__Feature204,Part__Feature205,Part__Feature206,Part__Feature207,Part__Feature208,Part__Feature209]
  Placement = pos=(18.6,-37,-18) rot=(0,0,1;3.14159rad)
FEATURE [Part::Feature] Part__Feature210  label="NEMA17"
  Placement = pos=(0,-37,-36) rot=(0,0,1;3.14159rad)
  shape: bbox 42.3 x 48.3 x 53.75 mm, 86 faces (baked)
FEATURE [Part::Feature] Part__Feature211  label="fan40x401"
  Placement = pos=(-67.6226,28.4181,-5) rot=(0,0,1;0rad)
  shape: bbox 40 x 40 x 10 mm, 57 faces (baked)
FEATURE [Part::Feature] Part__Feature212  label="wirnik"
  Placement = pos=(-67.6226,28.4181,5) rot=(1,0,0;3.14159rad)
  shape: bbox 37.02 x 37.02 x 7.019 mm, 112 faces (baked)
FEATURE [Part::Compound] Zesp_X_F3_X2_0142_X0_1
  Links = -> [Part__Feature211,Part__Feature212]
  Placement = pos=(0,-28,67) rot=(0,-1,0;1.5708rad)
FEATURE [Part::Feature] Part__Feature199  label="FAN35x35x10"
  Placement = pos=(-8.5,-0.5,1.4) rot=(0,-1,0;1.5708rad)
  shape: bbox 10 x 35 x 35 mm, 116 faces (baked)
FEATURE [Mesh::Feature] extruder
  Placement = pos=(-0.25,-18,1.9) rot=(-1,0,0;1.5708rad)
FEATURE [Part::Cylinder] Cylinder050  label="pushfit placeholder"
  Angle = 360
  AttacherType = Attacher::AttachEngine3D
  Height = 16
  Placement = pos=(7.5,-14.2,-4) rot=(1,0,0;1.5708rad)
  Radius = 3
FEATURE [Part::Cylinder] Cylinder051  label="extruder screw  L"
  Angle = 360
  AttacherType = Attacher::AttachEngine3D
  Height = 42
  Placement = pos=(-14.2,-35.8,-8) rot=(0,0,1;0rad)
  Radius = 1.5
FEATURE [Part::Cylinder] Cylinder052  label="extruder screw  R"
  Angle = 360
  AttacherType = Attacher::AttachEngine3D
  Height = 42
  Placement = pos=(16.8,-35.8,-8) rot=(0,0,1;0rad)
  Radius = 1.5
FEATURE [Part::Box] Box084  label="motor bracket base L lower"
  AttacherType = Attacher::AttachEngine3D
  Height = 25
  Length = 3
  Placement = pos=(-17.5,-30.2,-19) rot=(0,0,1;0rad)
  Width = 14.6
FEATURE [Part::Box] Box085  label="motor bracket base L upper"
  AttacherType = Attacher::AttachEngine3D
  Height = 3.5
  Length = 7
  Placement = pos=(-17.5,-40.2,2.5) rot=(0,0,1;0rad)
  Width = 10.6
FEATURE [Part::Box] Box086  label="motor bracket base R"
  AttacherType = Attacher::AttachEngine3D
  Height = 3.5
  Length = 8
  Placement = pos=(12.5,-40.2,2.5) rot=(0,0,1;0rad)
  Width = 32.6
FEATURE [Part::Chamfer] Chamfer  label="motor bracket base L upper chamfered"
  Base = -> Box085
  Edges = 1 edges r=4: [Edge7]
FEATURE [Part::MultiFuse] Fusion022  label="blower retention arm"
  Shapes = -> [Box080,Cylinder048,Box084,Chamfer]
FEATURE [Part::Cylinder] Cylinder053  label="cylinder for hole 9 - Groovemount L head seat"
  Angle = 360
  AttacherType = Attacher::AttachEngine3D
  Height = 4
  Placement = pos=(-20,-20,-2.5) rot=(1,0,0;1.5708rad)
  Radius = 4
FEATURE [Part::Cylinder] Cylinder054  label="cylinder for hole 3 - Motherboard head seat"
  Angle = 360
  AttacherType = Attacher::AttachEngine3D
  Height = 4
  Placement = pos=(-20,-20,-13.5) rot=(1,0,0;1.5708rad)
  Radius = 4
FEATURE [Part::Box] Box087  label="motor support"
  AttacherType = Attacher::AttachEngine3D
  Height = 6.5
  Length = 16
  Placement = pos=(-0.5,-30.2,-19) rot=(0,0,1;0rad)
  Width = 20.6
FEATURE [Part::MultiFuse] Fusion021  label="hexagon retention block"
  Shapes = -> [Box079,Box075,Box083,Box086,Box087]
FEATURE [Part::Box] Box088  label="fastener hole"
  AttacherType = Attacher::AttachEngine3D
  Height = 3
  Length = 42
  Placement = pos=(-21.5,-28.2,-17.5) rot=(0,0,1;0rad)
  Width = 3
FEATURE [Part::MultiFuse] Fusion020  label="hexagon retention block holes"
  Shapes = -> [Cylinder044,Cylinder043,Cylinder045,Box078,Cylinder046,Box082,Cylinder040,Cylinder047,Cylinder052,Box088]
FEATURE [Part::Cut] Cut012  label="hexagon retention block with holes"
  Base = -> Fusion021
  Tool = -> Fusion020
FEATURE [Part::Box] Box089  label="fastener hole001"
  AttacherType = Attacher::AttachEngine3D
  Height = 3
  Length = 42
  Placement = pos=(-21.5,-28.2,-17.5) rot=(0,0,1;0rad)
  Width = 3
FEATURE [Part::MultiFuse] Fusion023  label="blower retention holes"
  Shapes = -> [Cylinder043,Cylinder040,Cylinder049,Cylinder051,Cylinder053,Cylinder054,Box089]
FEATURE [Part::Cut] Cut013  label="blower retention arm with holes"
  Base = -> Fusion022
  Tool = -> Fusion023
note: 1 file-system path scrubbed to <path> (originals preserved in the JSON sidecar)
